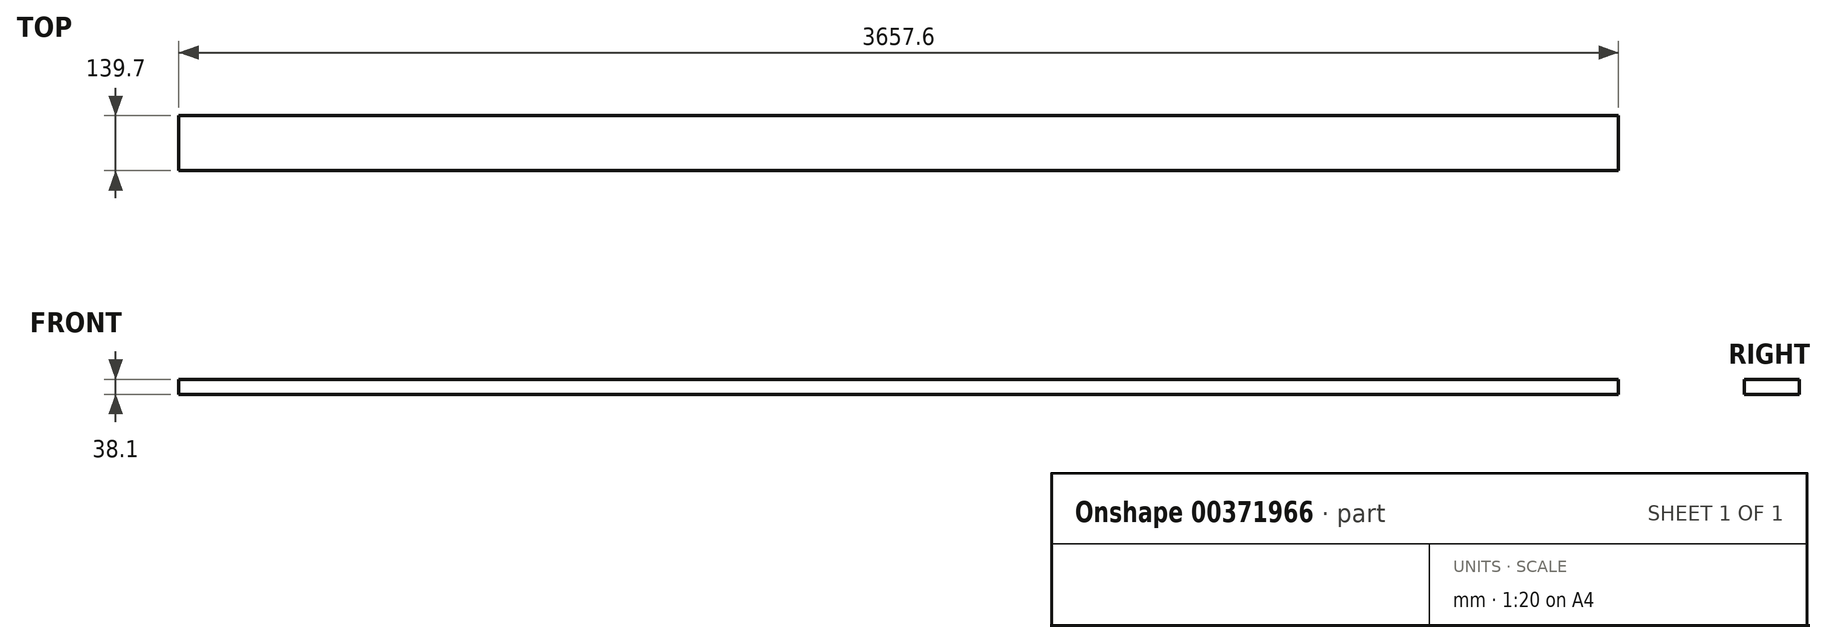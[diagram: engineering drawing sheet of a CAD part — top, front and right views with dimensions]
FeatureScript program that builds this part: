
annotation { "Feature Type Name" : "Feature", "Feature Type Description" : "" }
export const myFeature = defineFeature(function(context is Context, id is Id, definition is map)
    precondition{}
    {
        {
            var Q0;
            Q0=qCreatedBy(makeId("Top.planeOp"),FACE);
            var sketch = newSketch(context, id + "F0", { "sketchPlane" : qUnion([Q0])});
            skLineSegment(sketch, "E0.bottom", {"start": v(1828.8, -69.85) * mm, "end": v(-1828.8, -69.85) * mm});
            skLineSegment(sketch, "E0.top", {"start": v(1828.8, 69.85) * mm, "end": v(-1828.8, 69.85) * mm});
            skLineSegment(sketch, "E0.left", {"start": v(1828.8, -69.85) * mm, "end": v(1828.8, 69.85) * mm});
            skLineSegment(sketch, "E0.right", {"start": v(-1828.8, -69.85) * mm, "end": v(-1828.8, 69.85) * mm});
            skPoint(sketch, "E0.middle", {"position": v(0, 0) * mm});
            skSolve(sketch);
        }
        {
            var Q0;
            Q0=qSketchRegion(id+"F0",true);
            extrude(context, id + "F1", {"entities" : qUnion([Q0]), "oppositeDirection" : true, "depth" : 38.1 * mm});
        }
    });
